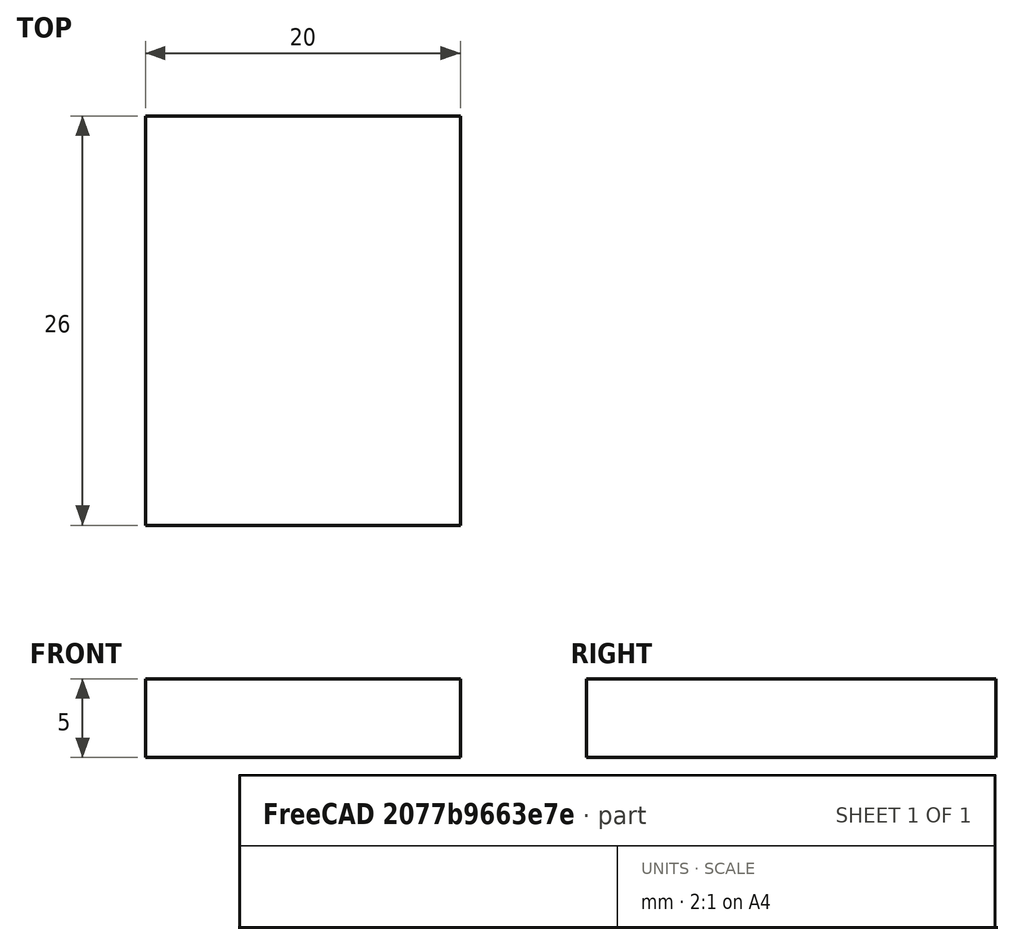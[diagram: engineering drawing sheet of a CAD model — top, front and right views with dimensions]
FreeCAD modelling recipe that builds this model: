
FCSTD DOCUMENT  (FreeCAD 0.16R6698 (Git))
Label: felt pad
License: All rights reserved
LicenseURL: http://en.wikipedia.org/wiki/All_rights_reserved
objects: Sketcher::SketchObject×1, PartDesign::Pad×1
note: 3 computed .brp shape members not serialized (recipe doc carries the construction recipe); baked Part::Feature solids carry a one-line shape summary decoded from their .brp

FEATURE [Sketcher::SketchObject] Sketch
  sketch-geometry (4):
    g0: LineSegment StartX=-13.4239 StartY=14.4732 StartZ=0 EndX=6.57609 EndY=14.4732 EndZ=0
    g1: LineSegment StartX=6.57609 StartY=14.4732 StartZ=0 EndX=6.57609 EndY=-11.5268 EndZ=0
    g2: LineSegment StartX=6.57609 StartY=-11.5268 StartZ=0 EndX=-13.4239 EndY=-11.5268 EndZ=0
    g3: LineSegment StartX=-13.4239 StartY=-11.5268 StartZ=0 EndX=-13.4239 EndY=14.4732 EndZ=0
  constraints (10):
    c: Coincident(g0,g1)
    c: Coincident(g1,g2)
    c: Coincident(g2,g3)
    c: Coincident(g3,g0)
    c: Horizontal(g0)
    c: Horizontal(g2)
    c: Vertical(g1)
    c: Vertical(g3)
    c: DistanceX(g0,g0) = 20
    c: DistanceY(g3,g3) = 26
FEATURE [PartDesign::Pad] Pad
  Length = 5
  Length2 = 100
  Sketch = -> Sketch
  Type = 0
